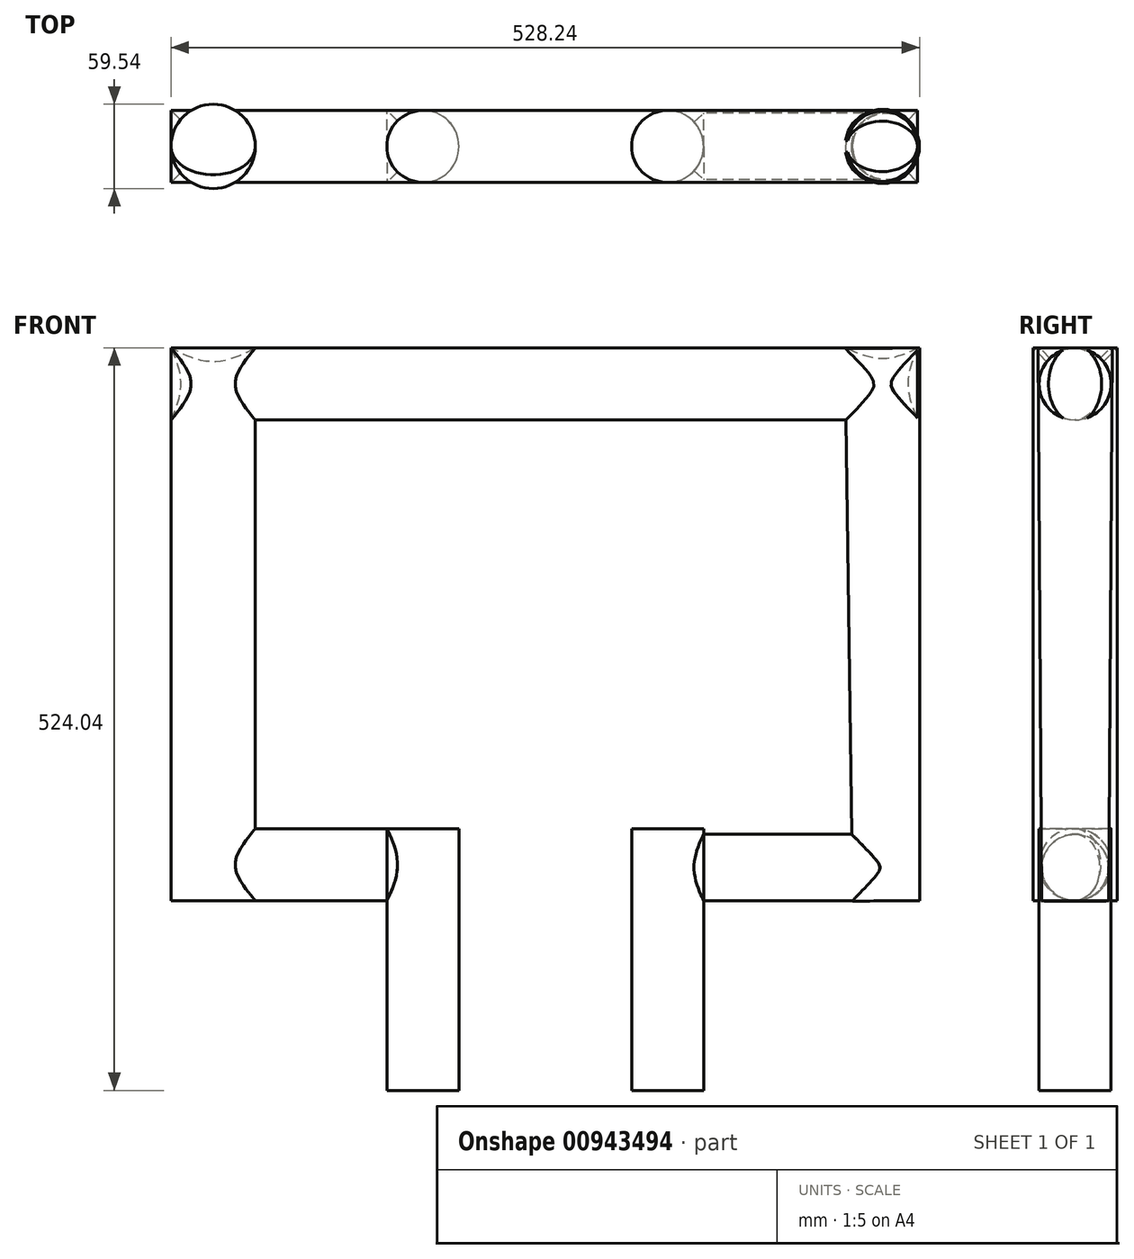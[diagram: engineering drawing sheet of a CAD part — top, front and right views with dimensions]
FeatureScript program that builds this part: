
annotation { "Feature Type Name" : "Feature", "Feature Type Description" : "" }
export const myFeature = defineFeature(function(context is Context, id is Id, definition is map)
    precondition{}
    {
        {
            var Q0;
            Q0=qCreatedBy(makeId("Front.planeOp"),FACE);
            var sketch = newSketch(context, id + "F0", { "sketchPlane" : qUnion([Q0])});
            skLineSegment(sketch, "E0", {"start": v(-325.04, 283.32) * mm, "end": v(-325.04, -106.8) * mm});
            skLineSegment(sketch, "E1", {"start": v(-325.04, -106.8) * mm, "end": v(-172.64, -106.8) * mm});
            skLineSegment(sketch, "E2", {"start": v(-172.64, -106.8) * mm, "end": v(-172.64, -240.72) * mm});
            skLineSegment(sketch, "E3", {"start": v(-172.64, -240.72) * mm, "end": v(-121.84, -240.72) * mm});
            skLineSegment(sketch, "E4", {"start": v(-121.84, -240.72) * mm, "end": v(-121.84, -106.8) * mm});
            skLineSegment(sketch, "E5", {"start": v(-121.84, -106.8) * mm, "end": v(-121.84, -56) * mm});
            skLineSegment(sketch, "E6", {"start": v(-121.84, -56) * mm, "end": v(-274.24, -56) * mm});
            skLineSegment(sketch, "E7", {"start": v(-274.24, -56) * mm, "end": v(-274.24, 232.52) * mm});
            skLineSegment(sketch, "E8", {"start": v(-274.24, 232.52) * mm, "end": v(152.4, 232.52) * mm});
            skLineSegment(sketch, "E9", {"start": v(152.4, 232.52) * mm, "end": v(152.4, -56) * mm});
            skLineSegment(sketch, "E10", {"start": v(152.4, -56) * mm, "end": v(0, -56) * mm});
            skLineSegment(sketch, "E11", {"start": v(0, -56) * mm, "end": v(0, -240.72) * mm});
            skLineSegment(sketch, "E12", {"start": v(0, -240.72) * mm, "end": v(50.8, -240.72) * mm});
            skLineSegment(sketch, "E13", {"start": v(50.8, -240.72) * mm, "end": v(50.8, -106.8) * mm});
            skLineSegment(sketch, "E14", {"start": v(50.8, -106.8) * mm, "end": v(203.2, -106.8) * mm});
            skLineSegment(sketch, "E15", {"start": v(203.2, -106.8) * mm, "end": v(203.2, 279.33) * mm});
            skLineSegment(sketch, "E16", {"start": v(-325.04, 283.32) * mm, "end": v(201.78, 283.32) * mm});
            skLineSegment(sketch, "E17", {"start": v(203.2, 279.33) * mm, "end": v(203.2, 283.32) * mm});
            skLineSegment(sketch, "E18", {"start": v(203.2, 283.32) * mm, "end": v(201.78, 283.32) * mm});
            skLineSegment(sketch, "E19", {"start": v(-274.24, 232.52) * mm, "end": v(-325.04, 283.32) * mm});
            skLineSegment(sketch, "E20", {"start": v(152.4, 232.52) * mm, "end": v(201.78, 283.32) * mm});
            skLineSegment(sketch, "E21", {"start": v(-299.64, 257.92) * mm, "end": v(177.09, 257.92) * mm});
            skLineSegment(sketch, "E22", {"start": v(-295.27, 253.54) * mm, "end": v(-295.27, -106.8) * mm});
            skLineSegment(sketch, "E23", {"start": v(-147.24, -240.72) * mm, "end": v(-147.24, -56) * mm});
            skLineSegment(sketch, "E24", {"start": v(-147.24, -81.4) * mm, "end": v(-295.27, -81.4) * mm});
            skPoint(sketch, "E24.startSnap0", {"position": v(-121.84, -81.4) * mm});
            skLineSegment(sketch, "E25", {"start": v(25.4, -240.72) * mm, "end": v(25.4, -56) * mm});
            skLineSegment(sketch, "E26", {"start": v(179.55, -106.8) * mm, "end": v(177.09, 257.92) * mm});
            skLineSegment(sketch, "E27", {"start": v(25.4, -83.35) * mm, "end": v(179.4, -83.35) * mm});
            skLineSegment(sketch, "E28", {"start": v(-172.64, -106.8) * mm, "end": v(-147.24, -81.4) * mm});
            skLineSegment(sketch, "E29", {"start": v(50.8, -106.8) * mm, "end": v(25.4, -83.35) * mm});
            skSolve(sketch);
        }
        {
            var Q0;
            {var subQ0=sQuery(id+"F0.wireOp",EDGE,"E16");Q0=makeQuery(id+"F0.imprint","IMPRINT",FACE,{"disambiguationData":[TD([[makeQuery(id+"F0.imprint","IMPRINT",EDGE,{"derivedFrom":subQ0}),-1.0]])]});}
            var Q1;
            Q1=sQuery(id+"F0.wireOp",EDGE,"E21");
            revolve(context, id + "F1", {"surfaceOperationType" : NewSurfaceOperationType.NEW, "entities" : qUnion([Q0]), "axis" : qUnion([Q1]), "revolveType" : RevolveType.FULL});
        }
        {
            var Q0;
            {var subQ1=sQuery(id+"F0.wireOp",EDGE,"E0");Q0=makeQuery(id+"F0.imprint","IMPRINT",FACE,{"disambiguationData":[TD([[makeQuery(id+"F0.imprint","IMPRINT",EDGE,{"derivedFrom":subQ1}),1.0]])]});}
            var Q1;
            Q1=sQuery(id+"F0.wireOp",EDGE,"E22");
            revolve(context, id + "F2", {"operationType" : NewBodyOperationType.ADD, "surfaceOperationType" : NewSurfaceOperationType.NEW, "entities" : qUnion([Q0]), "axis" : qUnion([Q1]), "revolveType" : RevolveType.FULL});
        }
        {
            var Q0;
            {var subQ1=sQuery(id+"F0.wireOp",EDGE,"E15");Q0=makeQuery(id+"F0.imprint","IMPRINT",FACE,{"disambiguationData":[TD([[makeQuery(id+"F0.imprint","IMPRINT",EDGE,{"derivedFrom":subQ1}),1.0]])]});}
            var Q1;
            Q1=sQuery(id+"F0.wireOp",EDGE,"E26");
            revolve(context, id + "F3", {"operationType" : NewBodyOperationType.ADD, "surfaceOperationType" : NewSurfaceOperationType.NEW, "entities" : qUnion([Q0]), "axis" : qUnion([Q1]), "revolveType" : RevolveType.FULL});
        }
        {
            var Q0;
            {var subQ4=sQuery(id+"F0.wireOp",EDGE,"E24");Q0=makeQuery(id+"F0.imprint","IMPRINT",FACE,{"disambiguationData":[TD([[makeQuery(id+"F0.imprint","IMPRINT",EDGE,{"derivedFrom":subQ4}),1.0]])]});}
            var Q1;
            Q1=sQuery(id+"F0.wireOp",EDGE,"E24");
            revolve(context, id + "F4", {"operationType" : NewBodyOperationType.ADD, "surfaceOperationType" : NewSurfaceOperationType.NEW, "entities" : qUnion([Q0]), "axis" : qUnion([Q1]), "revolveType" : RevolveType.FULL});
        }
        {
            var Q0;
            {var subQ4=sQuery(id+"F0.wireOp",EDGE,"E27");Q0=makeQuery(id+"F0.imprint","IMPRINT",FACE,{"disambiguationData":[TD([[makeQuery(id+"F0.imprint","IMPRINT",EDGE,{"derivedFrom":subQ4}),-1.0]])]});}
            var Q1;
            Q1=sQuery(id+"F0.wireOp",EDGE,"E27");
            revolve(context, id + "F5", {"operationType" : NewBodyOperationType.ADD, "surfaceOperationType" : NewSurfaceOperationType.NEW, "entities" : qUnion([Q0]), "axis" : qUnion([Q1]), "revolveType" : RevolveType.FULL});
        }
        {
            var Q0;
            {var subQ4=sQuery(id+"F0.wireOp",EDGE,"E4");Q0=makeQuery(id+"F0.imprint","IMPRINT",FACE,{"disambiguationData":[TD([[makeQuery(id+"F0.imprint","IMPRINT",EDGE,{"derivedFrom":subQ4}),1.0]])]});}
            var Q1;
            Q1=sQuery(id+"F0.wireOp",EDGE,"E23");
            revolve(context, id + "F6", {"operationType" : NewBodyOperationType.ADD, "surfaceOperationType" : NewSurfaceOperationType.NEW, "entities" : qUnion([Q0]), "axis" : qUnion([Q1]), "revolveType" : RevolveType.FULL});
        }
        {
            var Q0;
            {var subQ4=sQuery(id+"F0.wireOp",EDGE,"E11");Q0=makeQuery(id+"F0.imprint","IMPRINT",FACE,{"disambiguationData":[TD([[makeQuery(id+"F0.imprint","IMPRINT",EDGE,{"derivedFrom":subQ4}),1.0]])]});}
            var Q1;
            Q1=sQuery(id+"F0.wireOp",EDGE,"E25");
            revolve(context, id + "F7", {"operationType" : NewBodyOperationType.ADD, "surfaceOperationType" : NewSurfaceOperationType.NEW, "entities" : qUnion([Q0]), "axis" : qUnion([Q1]), "revolveType" : RevolveType.FULL});
        }
    });
